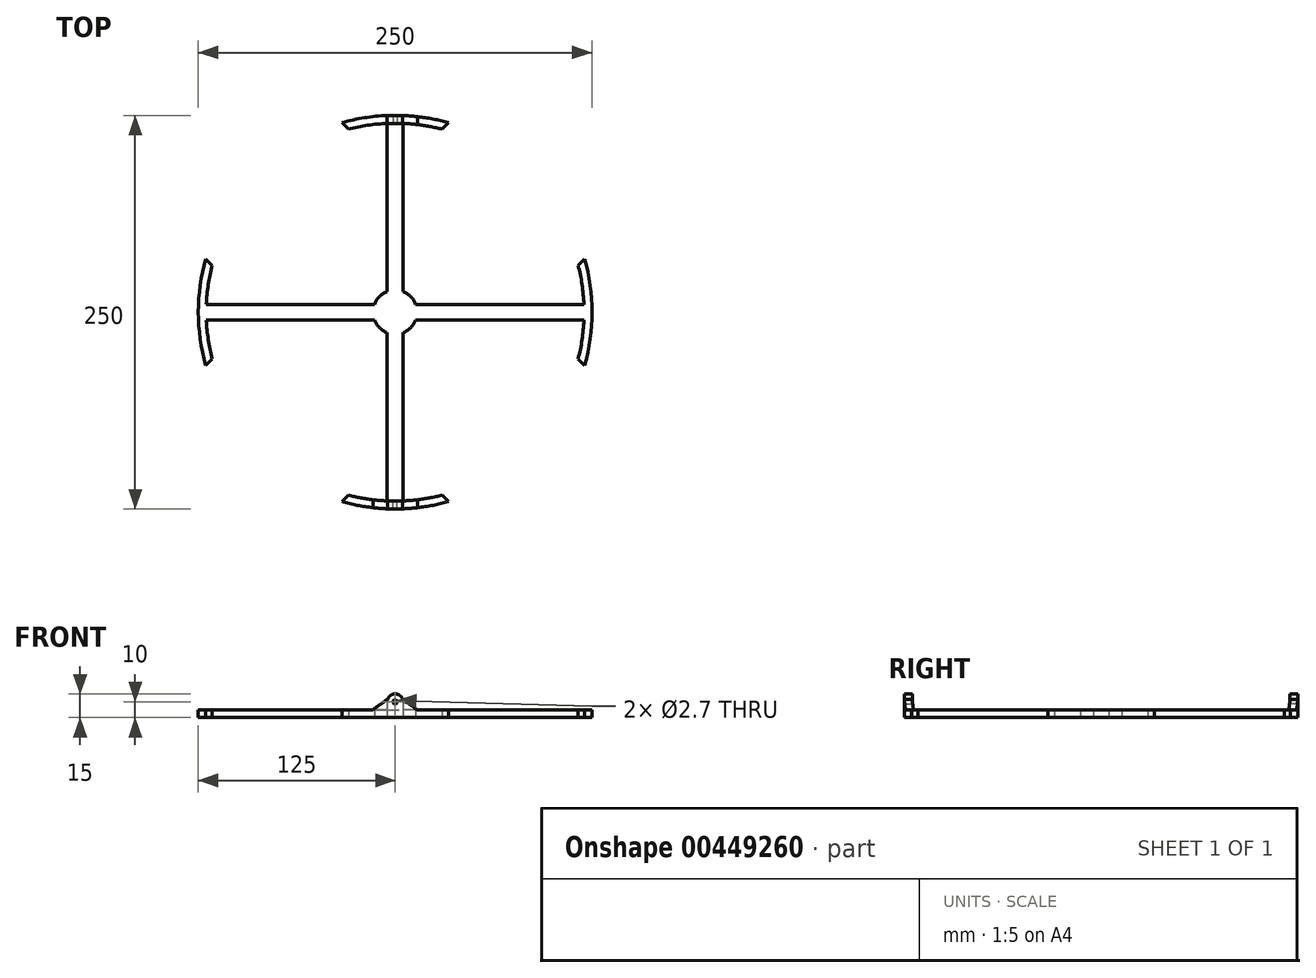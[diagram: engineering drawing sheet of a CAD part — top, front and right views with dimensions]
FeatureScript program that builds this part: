
annotation { "Feature Type Name" : "Feature", "Feature Type Description" : "" }
export const myFeature = defineFeature(function(context is Context, id is Id, definition is map)
    precondition{}
    {
        {
            var Q0;
            Q0=qCreatedBy(makeId("Top.planeOp"),FACE);
            var sketch = newSketch(context, id + "F0", { "sketchPlane" : qUnion([Q0])});
            skArc(sketch, "E0", {"start": v(-119.9, -5) * mm, "mid": v(-118.72, -17.46) * mm, "end": v(-116.26, -29.73) * mm});
            skArc(sketch, "E1", {"start": v(-33.82, -120.34) * mm, "mid": v(0, -125) * mm, "end": v(33.82, -120.34) * mm});
            skLineSegment(sketch, "E2.left", {"start": v(-5, 119.9) * mm, "end": v(-5, 5) * mm});
            skLineSegment(sketch, "E2.right", {"start": v(5, 119.9) * mm, "end": v(5, 5) * mm});
            skLineSegment(sketch, "E3.bottom", {"start": v(119.9, 5) * mm, "end": v(5, 5) * mm});
            skLineSegment(sketch, "E3.top", {"start": v(119.9, -5) * mm, "end": v(5, -5) * mm});
            skLineSegment(sketch, "E4.trimOffspring", {"start": v(-5, 5) * mm, "end": v(-119.9, 5) * mm});
            skLineSegment(sketch, "E5.trimOffspring", {"start": v(-5, -5) * mm, "end": v(-5, -119.9) * mm});
            skLineSegment(sketch, "E6.trimOffspring", {"start": v(-5, -5) * mm, "end": v(-119.9, -5) * mm});
            skLineSegment(sketch, "E7.trimOffspring", {"start": v(5, -5) * mm, "end": v(5, -119.9) * mm});
            skArc(sketch, "E8.trimOffspring", {"start": v(119.9, 5) * mm, "mid": v(118.72, 17.46) * mm, "end": v(116.26, 29.73) * mm});
            skArc(sketch, "E9.trimOffspring", {"start": v(-5, 119.9) * mm, "mid": v(-17.46, 118.72) * mm, "end": v(-29.73, 116.26) * mm});
            skArc(sketch, "E10.trimOffspring", {"start": v(5, -119.9) * mm, "mid": v(17.46, -118.72) * mm, "end": v(29.73, -116.26) * mm});
            skLineSegment(sketch, "E11", {"start": v(5, -119.9) * mm, "end": v(119.9, -5) * mm, "construction": true});
            skLineSegment(sketch, "E12", {"start": v(119.9, 5) * mm, "end": v(5, 119.9) * mm, "construction": true});
            skLineSegment(sketch, "E13", {"start": v(-5, 119.9) * mm, "end": v(-119.9, 5) * mm, "construction": true});
            skLineSegment(sketch, "E14", {"start": v(-119.9, -5) * mm, "end": v(-5, -119.9) * mm, "construction": true});
            skLineSegment(sketch, "E15", {"start": v(5, 5) * mm, "end": v(62.45, 62.45) * mm, "construction": true});
            skLineSegment(sketch, "E16", {"start": v(-5, 5) * mm, "end": v(-62.45, 62.45) * mm, "construction": true});
            skLineSegment(sketch, "E17", {"start": v(-5, -5) * mm, "end": v(-62.45, -62.45) * mm, "construction": true});
            skLineSegment(sketch, "E18", {"start": v(33.82, 120.34) * mm, "end": v(29.73, 116.26) * mm});
            skLineSegment(sketch, "E19", {"start": v(120.34, 33.82) * mm, "end": v(116.26, 29.73) * mm});
            skLineSegment(sketch, "E20", {"start": v(-29.73, -116.26) * mm, "end": v(-33.82, -120.34) * mm});
            skLineSegment(sketch, "E21", {"start": v(-116.26, -29.73) * mm, "end": v(-120.34, -33.82) * mm});
            skArc(sketch, "E22.trimOffspring", {"start": v(-29.73, -116.26) * mm, "mid": v(-17.46, -118.72) * mm, "end": v(-5, -119.9) * mm});
            skArc(sketch, "E23.trimOffspring", {"start": v(33.82, 120.34) * mm, "mid": v(0, 125) * mm, "end": v(-33.82, 120.34) * mm});
            skArc(sketch, "E24.trimOffspring", {"start": v(29.73, 116.26) * mm, "mid": v(17.46, 118.72) * mm, "end": v(5, 119.9) * mm});
            skLineSegment(sketch, "E25", {"start": v(-120.34, 33.82) * mm, "end": v(-116.26, 29.73) * mm});
            skLineSegment(sketch, "E26", {"start": v(116.26, -29.73) * mm, "end": v(120.34, -33.82) * mm});
            skLineSegment(sketch, "E27", {"start": v(29.73, -116.26) * mm, "end": v(33.82, -120.34) * mm});
            skArc(sketch, "E28.trimOffspring", {"start": v(-120.34, 33.82) * mm, "mid": v(-125, 0) * mm, "end": v(-120.34, -33.82) * mm});
            skArc(sketch, "E29.trimOffspring", {"start": v(-116.26, 29.73) * mm, "mid": v(-118.72, 17.46) * mm, "end": v(-119.9, 5) * mm});
            skArc(sketch, "E30.trimOffspring", {"start": v(116.26, -29.73) * mm, "mid": v(118.72, -17.46) * mm, "end": v(119.9, -5) * mm});
            skPoint(sketch, "E31.end.orphan", {"position": v(62.45, -62.45) * mm});
            skArc(sketch, "E32.trimOffspring", {"start": v(120.34, -33.82) * mm, "mid": v(125, 0) * mm, "end": v(120.34, 33.82) * mm});
            skLineSegment(sketch, "E33", {"start": v(-33.82, 120.34) * mm, "end": v(-29.73, 116.26) * mm});
            skSolve(sketch);
        }
        {
            var Q0;
            Q0=makeQuery(id+"F0.imprint","IMPRINT",FACE,{"disambiguationData":[TD([[makeQuery(id+"F0.imprint","IMPRINT",EDGE,{"derivedFrom":sQuery(id+"F0.wireOp",EDGE,"E0")}),-1.0]])]});
            extrude(context, id + "F1", {"entities" : qUnion([Q0]), "depth" : 5 * mm});
        }
        {
            var Q0;
            Q0=makeQuery(id+"F1.opExtrude","CAP_FACE",FACE,{"disambiguationData":[OSD([sQuery(id+"F0.wireOp",EDGE,"E0"),sQuery(id+"F0.wireOp",EDGE,"E1"),sQuery(id+"F0.wireOp",EDGE,"E2.left"),sQuery(id+"F0.wireOp",EDGE,"E2.right"),sQuery(id+"F0.wireOp",EDGE,"E3.bottom"),sQuery(id+"F0.wireOp",EDGE,"E3.top"),sQuery(id+"F0.wireOp",EDGE,"E4.trimOffspring"),sQuery(id+"F0.wireOp",EDGE,"E5.trimOffspring"),sQuery(id+"F0.wireOp",EDGE,"E6.trimOffspring"),sQuery(id+"F0.wireOp",EDGE,"E7.trimOffspring"),sQuery(id+"F0.wireOp",EDGE,"E8.trimOffspring"),sQuery(id+"F0.wireOp",EDGE,"E9.trimOffspring"),sQuery(id+"F0.wireOp",EDGE,"E10.trimOffspring"),sQuery(id+"F0.wireOp",EDGE,"E18"),sQuery(id+"F0.wireOp",EDGE,"E19"),sQuery(id+"F0.wireOp",EDGE,"E20"),sQuery(id+"F0.wireOp",EDGE,"E21"),sQuery(id+"F0.wireOp",EDGE,"E22.trimOffspring"),sQuery(id+"F0.wireOp",EDGE,"E23.trimOffspring"),sQuery(id+"F0.wireOp",EDGE,"E24.trimOffspring"),sQuery(id+"F0.wireOp",EDGE,"E25"),sQuery(id+"F0.wireOp",EDGE,"E26"),sQuery(id+"F0.wireOp",EDGE,"E27"),sQuery(id+"F0.wireOp",EDGE,"E28.trimOffspring"),sQuery(id+"F0.wireOp",EDGE,"E29.trimOffspring"),sQuery(id+"F0.wireOp",EDGE,"E30.trimOffspring"),sQuery(id+"F0.wireOp",EDGE,"E32.trimOffspring"),sQuery(id+"F0.wireOp",EDGE,"E33")])],"isStart":true});
            var sketch = newSketch(context, id + "F2", { "sketchPlane" : qUnion([Q0])});
            skCircle(sketch, "E34", {"center": v(0, 0) * mm, "radius": 14 * mm});
            skSolve(sketch);
        }
        {
            var Q0;
            {var subQ0=sQuery(id+"F2.wireOp",EDGE,"E34");var subQ1=makeQuery(id+"F1.opExtrude","CAP_EDGE",EDGE,{"disambiguationData":[OSD([sQuery(id+"F0.wireOp",EDGE,"E7.trimOffspring")])],"isStart":true});var subQ2=makeQuery(id+"F2.imprint","INTERSECT",VERTEX,{"derivedFrom":[subQ1,subQ0]});Q0=makeQuery(id+"F2.imprint","IMPRINT",FACE,{"disambiguationData":[TD([[makeQuery(id+"F2.imprint","IMPRINT",EDGE,{"disambiguationData":[TD([[subQ2,1.0]])],"derivedFrom":subQ0}),1.0]])]});}
            var Q1;
            {var subQ0=sQuery(id+"F2.wireOp",EDGE,"E34");var subQ1=makeQuery(id+"F1.opExtrude","CAP_EDGE",EDGE,{"disambiguationData":[OSD([sQuery(id+"F0.wireOp",EDGE,"E2.right")])],"isStart":true});var subQ2=makeQuery(id+"F2.imprint","INTERSECT",VERTEX,{"derivedFrom":[subQ1,subQ0]});Q1=makeQuery(id+"F2.imprint","IMPRINT",FACE,{"disambiguationData":[TD([[makeQuery(id+"F2.imprint","IMPRINT",EDGE,{"disambiguationData":[TD([[subQ2,-1.0]])],"derivedFrom":subQ0}),1.0]])]});}
            var Q2;
            {var subQ0=sQuery(id+"F2.wireOp",EDGE,"E34");var subQ1=makeQuery(id+"F1.opExtrude","CAP_EDGE",EDGE,{"disambiguationData":[OSD([sQuery(id+"F0.wireOp",EDGE,"E4.trimOffspring")])],"isStart":true});var subQ2=makeQuery(id+"F2.imprint","INTERSECT",VERTEX,{"derivedFrom":[subQ1,subQ0]});Q2=makeQuery(id+"F2.imprint","IMPRINT",FACE,{"disambiguationData":[TD([[makeQuery(id+"F2.imprint","IMPRINT",EDGE,{"disambiguationData":[TD([[subQ2,-1.0]])],"derivedFrom":subQ0}),1.0]])]});}
            var Q3;
            {var subQ0=sQuery(id+"F2.wireOp",EDGE,"E34");var subQ1=makeQuery(id+"F1.opExtrude","CAP_EDGE",EDGE,{"disambiguationData":[OSD([sQuery(id+"F0.wireOp",EDGE,"E5.trimOffspring")])],"isStart":true});var subQ2=makeQuery(id+"F2.imprint","INTERSECT",VERTEX,{"derivedFrom":[subQ1,subQ0]});Q3=makeQuery(id+"F2.imprint","IMPRINT",FACE,{"disambiguationData":[TD([[makeQuery(id+"F2.imprint","IMPRINT",EDGE,{"disambiguationData":[TD([[subQ2,-1.0]])],"derivedFrom":subQ0}),1.0]])]});}
            extrude(context, id + "F3", {"entities" : qUnion([Q0, Q1, Q2, Q3]), "operationType" : NewBodyOperationType.ADD, "oppositeDirection" : true, "depth" : 5 * mm});
        }
        {
            var Q0;
            {var subQ0=sQuery(id+"F2.wireOp",EDGE,"E34");var subQ1=sQuery(id+"F0.wireOp",EDGE,"E3.bottom");var subQ2=sQuery(id+"F0.wireOp",EDGE,"E2.right");var subQ3=sQuery(id+"F0.wireOp",EDGE,"E4.trimOffspring");var subQ4=sQuery(id+"F0.wireOp",EDGE,"E2.left");var subQ5=sQuery(id+"F0.wireOp",EDGE,"E6.trimOffspring");var subQ6=sQuery(id+"F0.wireOp",EDGE,"E5.trimOffspring");var subQ7=sQuery(id+"F0.wireOp",EDGE,"E7.trimOffspring");var subQ8=sQuery(id+"F0.wireOp",EDGE,"E3.top");Q0=makeQuery(id+"F3.boolean.opBoolean","MERGE",FACE,{"derivedFrom":[makeQuery(id+"F1.opExtrude","CAP_FACE",FACE,{"disambiguationData":[OSD([sQuery(id+"F0.wireOp",EDGE,"E0"),sQuery(id+"F0.wireOp",EDGE,"E1"),subQ4,subQ2,subQ1,subQ8,subQ3,subQ6,subQ5,subQ7,sQuery(id+"F0.wireOp",EDGE,"E8.trimOffspring"),sQuery(id+"F0.wireOp",EDGE,"E9.trimOffspring"),sQuery(id+"F0.wireOp",EDGE,"E10.trimOffspring"),sQuery(id+"F0.wireOp",EDGE,"E18"),sQuery(id+"F0.wireOp",EDGE,"E19"),sQuery(id+"F0.wireOp",EDGE,"E20"),sQuery(id+"F0.wireOp",EDGE,"E21"),sQuery(id+"F0.wireOp",EDGE,"E22.trimOffspring"),sQuery(id+"F0.wireOp",EDGE,"E23.trimOffspring"),sQuery(id+"F0.wireOp",EDGE,"E24.trimOffspring"),sQuery(id+"F0.wireOp",EDGE,"E25"),sQuery(id+"F0.wireOp",EDGE,"E26"),sQuery(id+"F0.wireOp",EDGE,"E27"),sQuery(id+"F0.wireOp",EDGE,"E28.trimOffspring"),sQuery(id+"F0.wireOp",EDGE,"E29.trimOffspring"),sQuery(id+"F0.wireOp",EDGE,"E30.trimOffspring"),sQuery(id+"F0.wireOp",EDGE,"E32.trimOffspring"),sQuery(id+"F0.wireOp",EDGE,"E33")])],"isStart":false}),makeQuery(id+"F3.opExtrude","CAP_FACE",FACE,{"disambiguationData":[OSD([subQ8,subQ7,subQ0])],"isStart":false}),makeQuery(id+"F3.opExtrude","CAP_FACE",FACE,{"disambiguationData":[OSD([subQ6,subQ5,subQ0])],"isStart":false}),makeQuery(id+"F3.opExtrude","CAP_FACE",FACE,{"disambiguationData":[OSD([subQ4,subQ3,subQ0])],"isStart":false}),makeQuery(id+"F3.opExtrude","CAP_FACE",FACE,{"disambiguationData":[OSD([subQ2,subQ1,subQ0])],"isStart":false})]});}
            var sketch = newSketch(context, id + "F4", { "sketchPlane" : qUnion([Q0])});
            skLineSegment(sketch, "E35", {"start": v(-5, 119.9) * mm, "end": v(5, 119.9) * mm});
            skLineSegment(sketch, "E36", {"start": v(-5, -119.9) * mm, "end": v(5, -119.9) * mm});
            skLineSegment(sketch, "E37", {"start": v(-5, 119.9) * mm, "end": v(-5, 124.9) * mm});
            skLineSegment(sketch, "E38", {"start": v(5, 119.9) * mm, "end": v(5, 124.9) * mm});
            skLineSegment(sketch, "E39", {"start": v(-5, -119.9) * mm, "end": v(-5, -124.9) * mm});
            skLineSegment(sketch, "E40", {"start": v(5, -119.9) * mm, "end": v(5, -124.9) * mm});
            skSolve(sketch);
        }
        {
            var Q0;
            Q0=makeQuery(id+"F4.imprint","IMPRINT",FACE,{"disambiguationData":[TD([[makeQuery(id+"F4.imprint","IMPRINT",EDGE,{"derivedFrom":sQuery(id+"F4.wireOp",EDGE,"E35")}),1.0]])]});
            var Q1;
            Q1=makeQuery(id+"F4.imprint","IMPRINT",FACE,{"disambiguationData":[TD([[makeQuery(id+"F4.imprint","IMPRINT",EDGE,{"derivedFrom":sQuery(id+"F4.wireOp",EDGE,"E36")}),-1.0]])]});
            extrude(context, id + "F5", {"entities" : qUnion([Q0, Q1]), "operationType" : NewBodyOperationType.ADD, "depth" : 10 * mm});
        }
        {
            var Q0;
            Q0=makeQuery(id+"F5.opExtrude","SWEPT_FACE",FACE,{"disambiguationData":[OSD([sQuery(id+"F4.wireOp",EDGE,"E36")])]});
            var sketch = newSketch(context, id + "F6", { "sketchPlane" : qUnion([Q0])});
            skCircle(sketch, "E41", {"center": v(0, 10) * mm, "radius": 1.35 * mm});
            skSolve(sketch);
        }
        {
            var Q0;
            Q0=makeQuery(id+"F6.imprint","IMPRINT",FACE,{"disambiguationData":[TD([[makeQuery(id+"F6.imprint","IMPRINT",EDGE,{"derivedFrom":sQuery(id+"F6.wireOp",EDGE,"E41")}),1.0]])]});
            extrude(context, id + "F7", {"entities" : qUnion([Q0]), "operationType" : NewBodyOperationType.REMOVE, "endBound" : BoundingType.THROUGH_ALL, "oppositeDirection" : true, "depth" : 25 * mm});
        }
        {
            var Q0;
            Q0=makeQuery(id+"F5.opExtrude","SWEPT_FACE",FACE,{"disambiguationData":[OSD([sQuery(id+"F4.wireOp",EDGE,"E35")])]});
            var sketch = newSketch(context, id + "F8", { "sketchPlane" : qUnion([Q0])});
            skCircle(sketch, "E42", {"center": v(0, 10) * mm, "radius": 1.35 * mm});
            skSolve(sketch);
        }
        {
            var Q0;
            Q0=makeQuery(id+"F8.imprint","IMPRINT",FACE,{"disambiguationData":[TD([[makeQuery(id+"F8.imprint","IMPRINT",EDGE,{"derivedFrom":sQuery(id+"F8.wireOp",EDGE,"E42")}),1.0]])]});
            extrude(context, id + "F9", {"entities" : qUnion([Q0]), "operationType" : NewBodyOperationType.REMOVE, "oppositeDirection" : true, "depth" : 25 * mm});
        }
        {
            var Q0;
            Q0=makeQuery(id+"F5.opExtrude","CAP_EDGE",EDGE,{"disambiguationData":[OSD([sQuery(id+"F4.wireOp",EDGE,"E39")])],"isStart":false});
            var Q1;
            Q1=makeQuery(id+"F5.opExtrude","CAP_EDGE",EDGE,{"disambiguationData":[OSD([sQuery(id+"F4.wireOp",EDGE,"E40")])],"isStart":false});
            var Q2;
            Q2=makeQuery(id+"F5.opExtrude","CAP_EDGE",EDGE,{"disambiguationData":[OSD([sQuery(id+"F4.wireOp",EDGE,"E37")])],"isStart":false});
            var Q3;
            Q3=makeQuery(id+"F5.opExtrude","CAP_EDGE",EDGE,{"disambiguationData":[OSD([sQuery(id+"F4.wireOp",EDGE,"E38")])],"isStart":false});
            fillet(context, id + "F10", {"entities" : qUnion([Q0, Q1, Q2, Q3]), "radius" : 5 * mm, "tangentPropagation" : true, "allowEdgeOverflow" : false});
        }
        {
            var Q0;
            Q0=makeQuery(id+"F5.opExtrude","CAP_EDGE",EDGE,{"disambiguationData":[OSD([sQuery(id+"F4.wireOp",EDGE,"E38")])],"isStart":true});
            var Q1;
            Q1=makeQuery(id+"F5.opExtrude","CAP_EDGE",EDGE,{"disambiguationData":[OSD([sQuery(id+"F4.wireOp",EDGE,"E37")])],"isStart":true});
            var Q2;
            Q2=makeQuery(id+"F5.opExtrude","CAP_EDGE",EDGE,{"disambiguationData":[OSD([sQuery(id+"F4.wireOp",EDGE,"E40")])],"isStart":true});
            var Q3;
            Q3=makeQuery(id+"F5.opExtrude","CAP_EDGE",EDGE,{"disambiguationData":[OSD([sQuery(id+"F4.wireOp",EDGE,"E39")])],"isStart":true});
            chamfer(context, id + "F11", {"entities" : qUnion([Q0, Q1, Q2, Q3]), "width" : 10 * mm, "tangentPropagation" : true});
        }
    });
